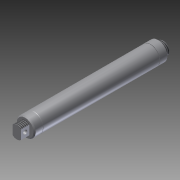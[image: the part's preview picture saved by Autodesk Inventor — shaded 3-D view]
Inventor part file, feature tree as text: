
AUTODESK INVENTOR PART (.ipt)
format: ipt  version: 2012 (Build 160160000, 160)  size: 159,232 bytes
history: native  units: in
note: dims shown in document units (in); Inventor stores cm internally (conversion verified against a paired STEP export)
features: extrude x7, sketch x3, thread x3, fillet x2, chamfer x2
ambient origin geometry x8: Origin, YZ Plane, XZ Plane, XY Plane, X Axis, Y Axis, Z Axis, Center Point
bodies: Solid1 (feature_tree)
feature tree (17):
  sketch  "Sketch1"  dims[d2=1.0in d3=1.125in d4=0.5in]
  extrude  "Extrusion1"  Depth=1.125in
  fillet  "Fillet1"  Radius=0.5in
  extrude  "Extrusion2"  Depth=0.559in
  extrude  "Extrusion3"  Depth=0.375in
  chamfer  "Chamfer1"  Distance=7.0in
  thread  "Thread1"  [1 undecoded]
  thread  "Thread2"  [1 undecoded]
  sketch  "Sketch2"  dims[d5=0.25in d6=0.559in]
  extrude  "Extrusion4"  Depth=1.0in TaperAngle=0.0deg
  extrude  "Extrusion5"  Depth=0.0625in TaperAngle=45.0deg
  fillet  "Fillet2"  Radius=1.0in
  extrude  "Extrusion6"  Depth=1.0in TaperAngle=0.0deg
  chamfer  "Chamfer2"  Distance=0.75in
  thread  "Thread3"  [1 undecoded]
  extrude  "Extrusion7"  Depth=0.25in
  sketch  "Sketch3"  dims[d7=0.2795in d8=0.375in d10=7.0in d11=0.0in d12=0.0312in d13=0.5in d14=0.0in d15=1.0in d16=0.0in d17=0.0625in d18=0.125in d19=45.0deg d20=1.0in d21=0.0in d22=1.0in d23=0.0in d24=0.75in d25=0.3125in d26=0.25in d27=0.5in d28=0.0in d29=0.75in d30=0.0in d31=0.0075in d32=0.75in d33=0.0in d34=0.0625in d35=0.125in d36=45.0deg d37=1.0in d38=0.0in d39=0.25in d40=0.2795in d41=0.559in d42=0.25in d43=1.0in d44=0.0in]
note: 3 required parameter values undecoded (feature->parameter linkage not recoverable at this tier; creation-order binding heuristic only, values carry confidence <= 0.55)
